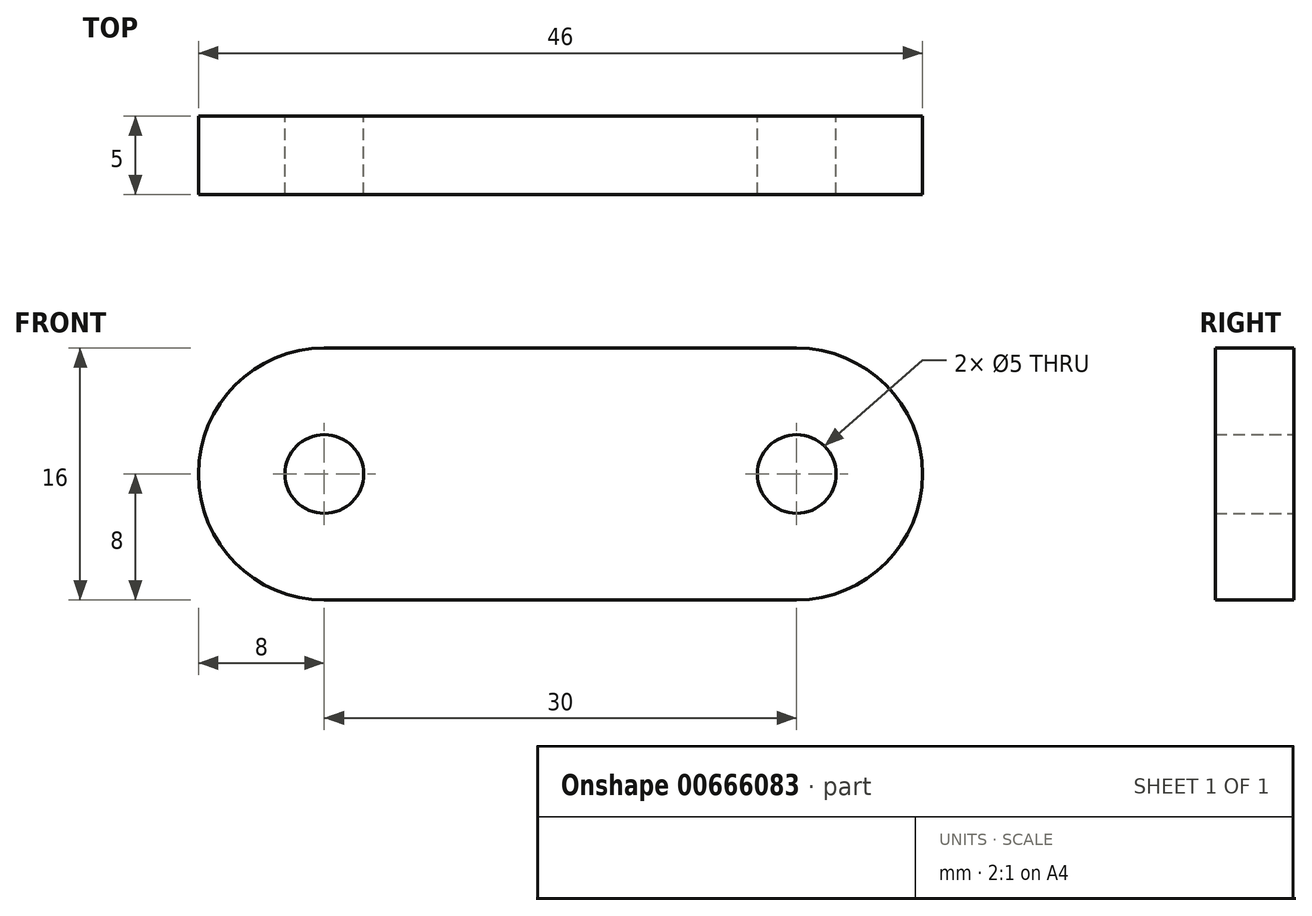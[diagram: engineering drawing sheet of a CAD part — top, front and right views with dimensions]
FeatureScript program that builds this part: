
annotation { "Feature Type Name" : "Feature", "Feature Type Description" : "" }
export const myFeature = defineFeature(function(context is Context, id is Id, definition is map)
    precondition{}
    {
        {
            var Q0;
            Q0=qCreatedBy(makeId("Front.planeOp"),FACE);
            var sketch = newSketch(context, id + "F0", { "sketchPlane" : qUnion([Q0])});
            skLineSegment(sketch, "E0.bottom", {"start": v(-15, 8) * mm, "end": v(15, 8) * mm});
            skLineSegment(sketch, "E0.top", {"start": v(-15, -8) * mm, "end": v(15, -8) * mm});
            skArc(sketch, "E1", {"start": v(-15, 8) * mm, "mid": v(-23, 0) * mm, "end": v(-15, -8) * mm});
            skArc(sketch, "E2", {"start": v(15, -8) * mm, "mid": v(23, 0) * mm, "end": v(15, 8) * mm});
            skCircle(sketch, "E3", {"center": v(-15, 0) * mm, "radius": 2.5 * mm});
            skCircle(sketch, "E4", {"center": v(15, 0) * mm, "radius": 2.5 * mm});
            skSolve(sketch);
        }
        {
            var Q0;
            Q0=makeQuery(id+"F0.imprint","IMPRINT",FACE,{"disambiguationData":[TD([[makeQuery(id+"F0.imprint","IMPRINT",EDGE,{"derivedFrom":sQuery(id+"F0.wireOp",EDGE,"E0.bottom")}),-1.0]])]});
            extrude(context, id + "F1", {"entities" : qUnion([Q0]), "depth" : 5 * mm, "offsetDistance" : 25 * mm});
        }
    });
